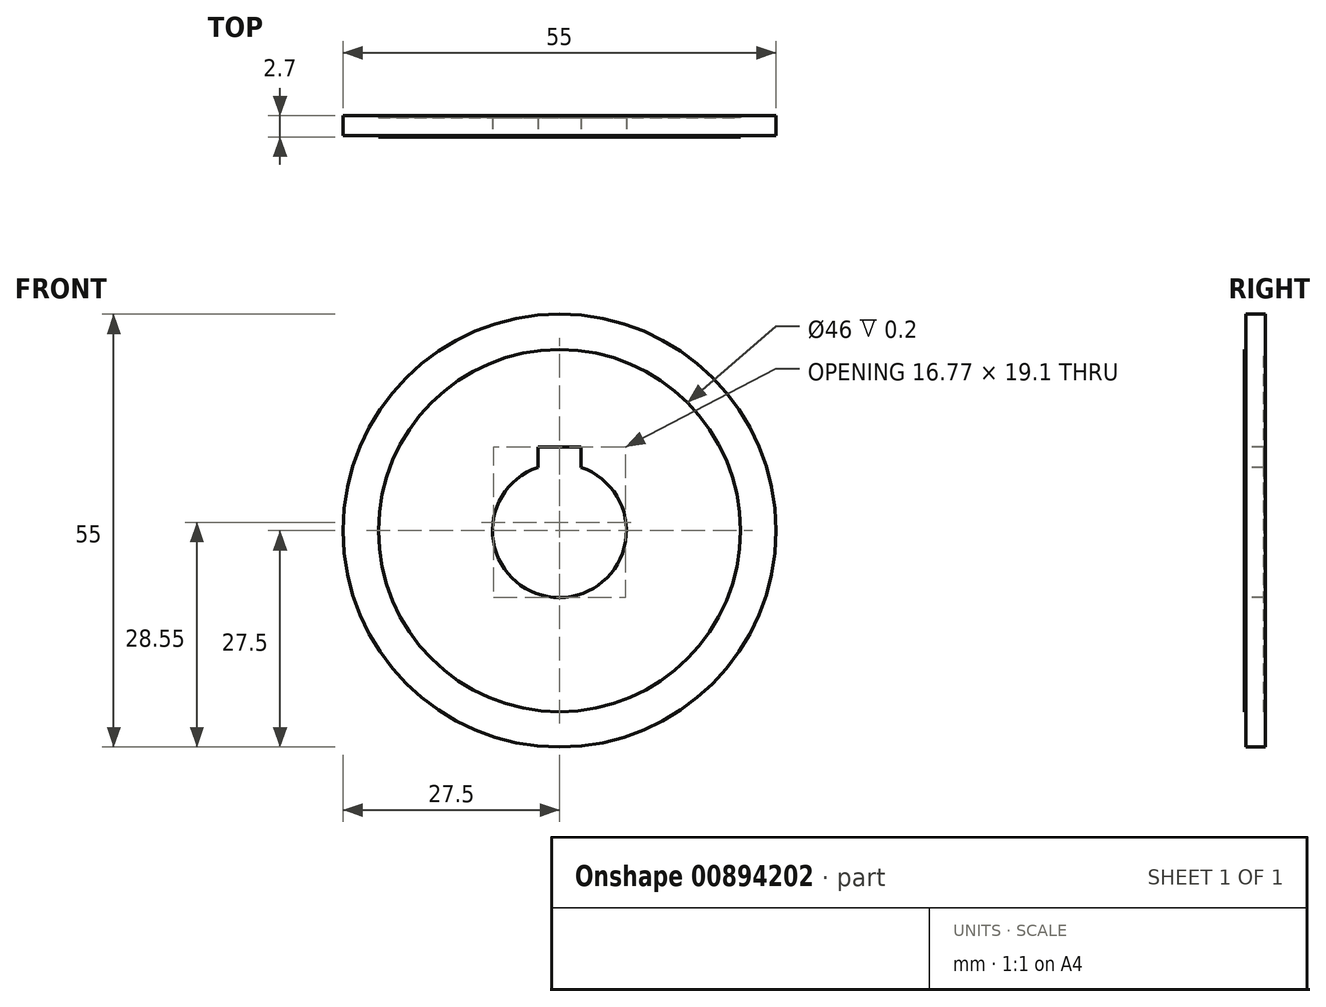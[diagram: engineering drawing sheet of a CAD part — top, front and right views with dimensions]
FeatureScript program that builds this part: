
annotation { "Feature Type Name" : "Feature", "Feature Type Description" : "" }
export const myFeature = defineFeature(function(context is Context, id is Id, definition is map)
    precondition{}
    {
        {
            var Q0;
            Q0=qCreatedBy(makeId("Right.planeOp"),FACE);
            var sketch = newSketch(context, id + "F0", { "sketchPlane" : qUnion([Q0])});
            skLineSegment(sketch, "E0", {"start": v(0, 0) * mm, "end": v(0, 8.5) * mm, "construction": true});
            skLineSegment(sketch, "E1", {"start": v(0, 8.5) * mm, "end": v(0, 23) * mm});
            skLineSegment(sketch, "E2", {"start": v(2.5, 23) * mm, "end": v(2.5, 8.5) * mm});
            skLineSegment(sketch, "E3", {"start": v(2.5, 8.5) * mm, "end": v(0, 8.5) * mm});
            skLineSegment(sketch, "E4", {"start": v(0, 0) * mm, "end": v(2.5, 0) * mm});
            skLineSegment(sketch, "E5", {"start": v(0, 23) * mm, "end": v(0.2, 23) * mm});
            skLineSegment(sketch, "E6", {"start": v(0.2, 23) * mm, "end": v(0.2, 27.5) * mm});
            skLineSegment(sketch, "E7", {"start": v(0.2, 27.5) * mm, "end": v(2.7, 27.5) * mm});
            skLineSegment(sketch, "E8", {"start": v(2.7, 27.5) * mm, "end": v(2.7, 23) * mm});
            skLineSegment(sketch, "E9", {"start": v(2.7, 23) * mm, "end": v(2.5, 23) * mm});
            skSolve(sketch);
        }
        {
            var Q0;
            Q0 = qSketchRegion(id + "F0", true);
            var Q1;
            Q1=sQuery(id+"F0.wireOp",EDGE,"E4");
            revolve(context, id + "F1", {"surfaceOperationType" : NewSurfaceOperationType.NEW, "entities" : qUnion([Q0]), "axis" : qUnion([Q1]), "revolveType" : RevolveType.FULL});
        }
        {
            var Q0;
            Q0=qCreatedBy(makeId("Front.planeOp"),FACE);
            var sketch = newSketch(context, id + "F2", { "sketchPlane" : qUnion([Q0])});
            skLineSegment(sketch, "E10", {"start": v(0, 0) * mm, "end": v(0, 10.6) * mm, "construction": true});
            skLineSegment(sketch, "E11", {"start": v(-2.75, 10.6) * mm, "end": v(2.75, 10.6) * mm});
            skLineSegment(sketch, "E12", {"start": v(2.75, 10.6) * mm, "end": v(2.75, 8.04) * mm});
            skLineSegment(sketch, "E13", {"start": v(-2.75, 10.6) * mm, "end": v(-2.75, 8.04) * mm});
            skArc(sketch, "E14", {"start": v(2.75, 8.04) * mm, "mid": v(0, 8.5) * mm, "end": v(-2.75, 8.04) * mm});
            skSolve(sketch);
        }
        {
            var Q0;
            Q0 = qSketchRegion(id + "F2", true);
            extrude(context, id + "F3", {"entities" : qUnion([Q0]), "operationType" : NewBodyOperationType.REMOVE, "endBound" : BoundingType.THROUGH_ALL, "oppositeDirection" : true, "depth" : 25 * mm, "offsetDistance" : 25 * mm});
        }
    });
